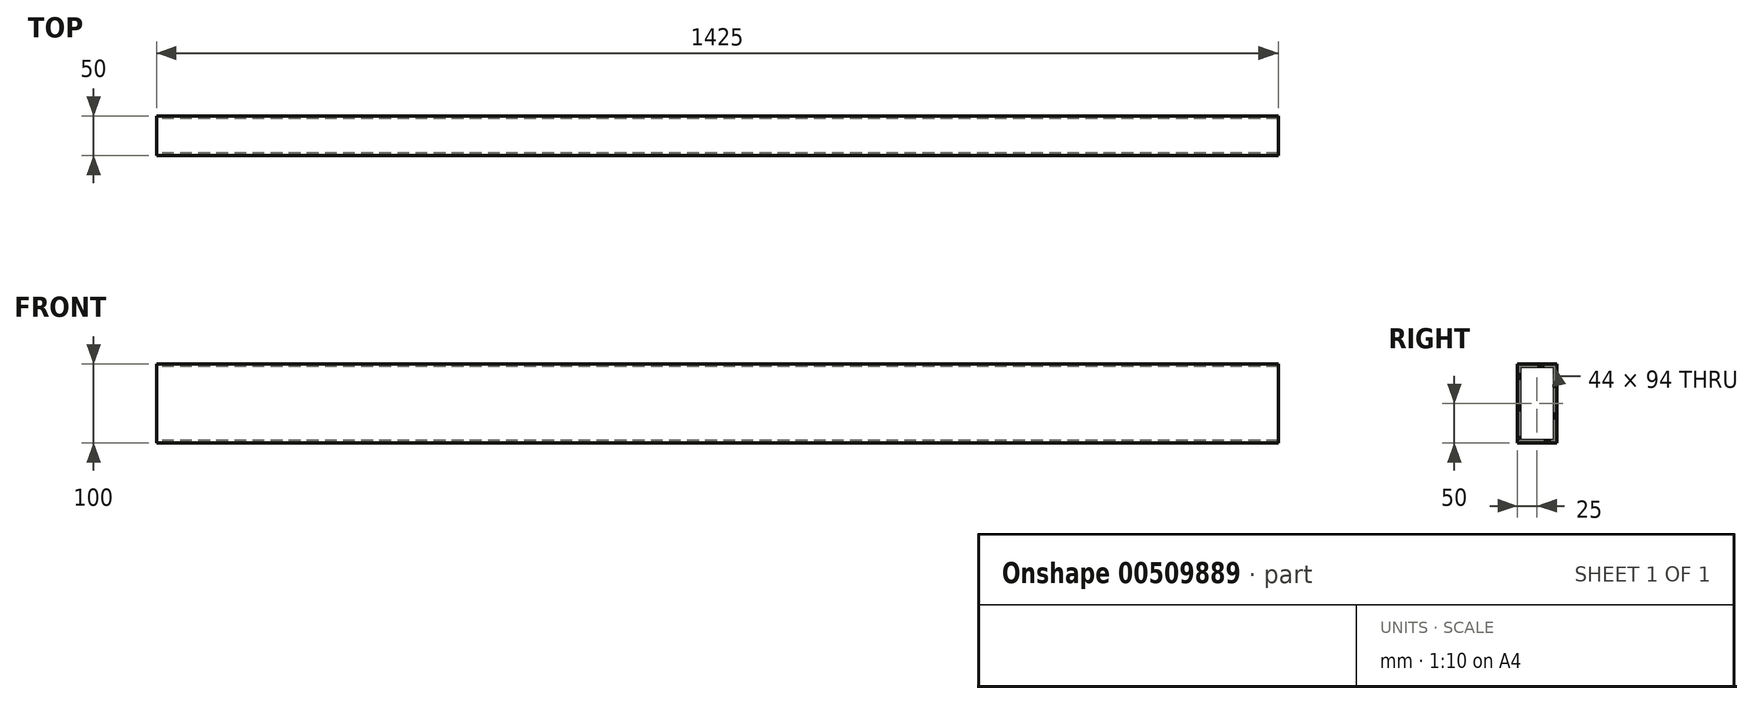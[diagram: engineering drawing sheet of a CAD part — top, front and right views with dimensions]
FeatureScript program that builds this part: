
annotation { "Feature Type Name" : "Feature", "Feature Type Description" : "" }
export const myFeature = defineFeature(function(context is Context, id is Id, definition is map)
    precondition{}
    {
        {
            var Q0;
            Q0=qCreatedBy(makeId("Right.planeOp"),FACE);
            var sketch = newSketch(context, id + "F0", { "sketchPlane" : qUnion([Q0])});
            skLineSegment(sketch, "E0.bottom", {"start": v(25, -50) * mm, "end": v(-25, -50) * mm});
            skLineSegment(sketch, "E0.top", {"start": v(25, 50) * mm, "end": v(-25, 50) * mm});
            skLineSegment(sketch, "E0.left", {"start": v(25, -50) * mm, "end": v(25, 50) * mm});
            skLineSegment(sketch, "E0.right", {"start": v(-25, -50) * mm, "end": v(-25, 50) * mm});
            skPoint(sketch, "E0.middle", {"position": v(0, 0) * mm});
            skLineSegment(sketch, "E1.bottom", {"start": v(22, -47) * mm, "end": v(-22, -47) * mm});
            skLineSegment(sketch, "E1.top", {"start": v(22, 47) * mm, "end": v(-22, 47) * mm});
            skLineSegment(sketch, "E1.left", {"start": v(22, -47) * mm, "end": v(22, 47) * mm});
            skLineSegment(sketch, "E1.right", {"start": v(-22, -47) * mm, "end": v(-22, 47) * mm});
            skSolve(sketch);
        }
        {
            var Q0;
            Q0=makeQuery(id+"F0.imprint","IMPRINT",FACE,{"disambiguationData":[TD([[makeQuery(id+"F0.imprint","IMPRINT",EDGE,{"derivedFrom":sQuery(id+"F0.wireOp",EDGE,"E0.bottom")}),-1.0]])]});
            extrude(context, id + "F1", {"entities" : qUnion([Q0]), "depth" : 1425 * mm, "offsetDistance" : 25 * mm});
        }
    });
